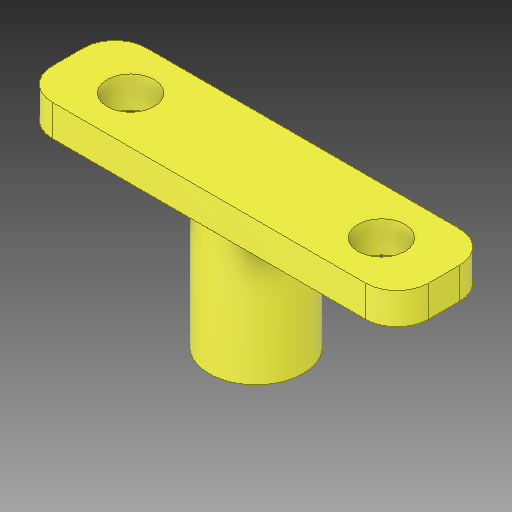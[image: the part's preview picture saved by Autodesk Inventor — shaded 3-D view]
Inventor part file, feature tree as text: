
AUTODESK INVENTOR PART (.ipt)
format: ipt  version: 2018.2 (Build 222227000, 227)  size: 127,488 bytes
history: native  units: mm
features: extrude x2, sketch x1, fillet x1
ambient origin geometry x8: Origin, YZ Plane, XZ Plane, XY Plane, X Axis, Y Axis, Z Axis, Center Point
bodies: Solid1 (feature_tree)
feature tree (4):
  sketch  "Sketch1"  dims[d0=3.0mm d1=3.0mm d2=8.0mm d3=8.0mm d4=24.0mm d5=6.0mm d6=2.8mm d7=2.0mm d8=0.0mm d9=8.0mm d10=0.0mm d12=2.0mm]
  extrude  "Extrusion1"  Depth=3.0mm
  extrude  "Extrusion2"  Depth=8.0mm
  fillet  "Fillet2"  Radius=8.0mm
